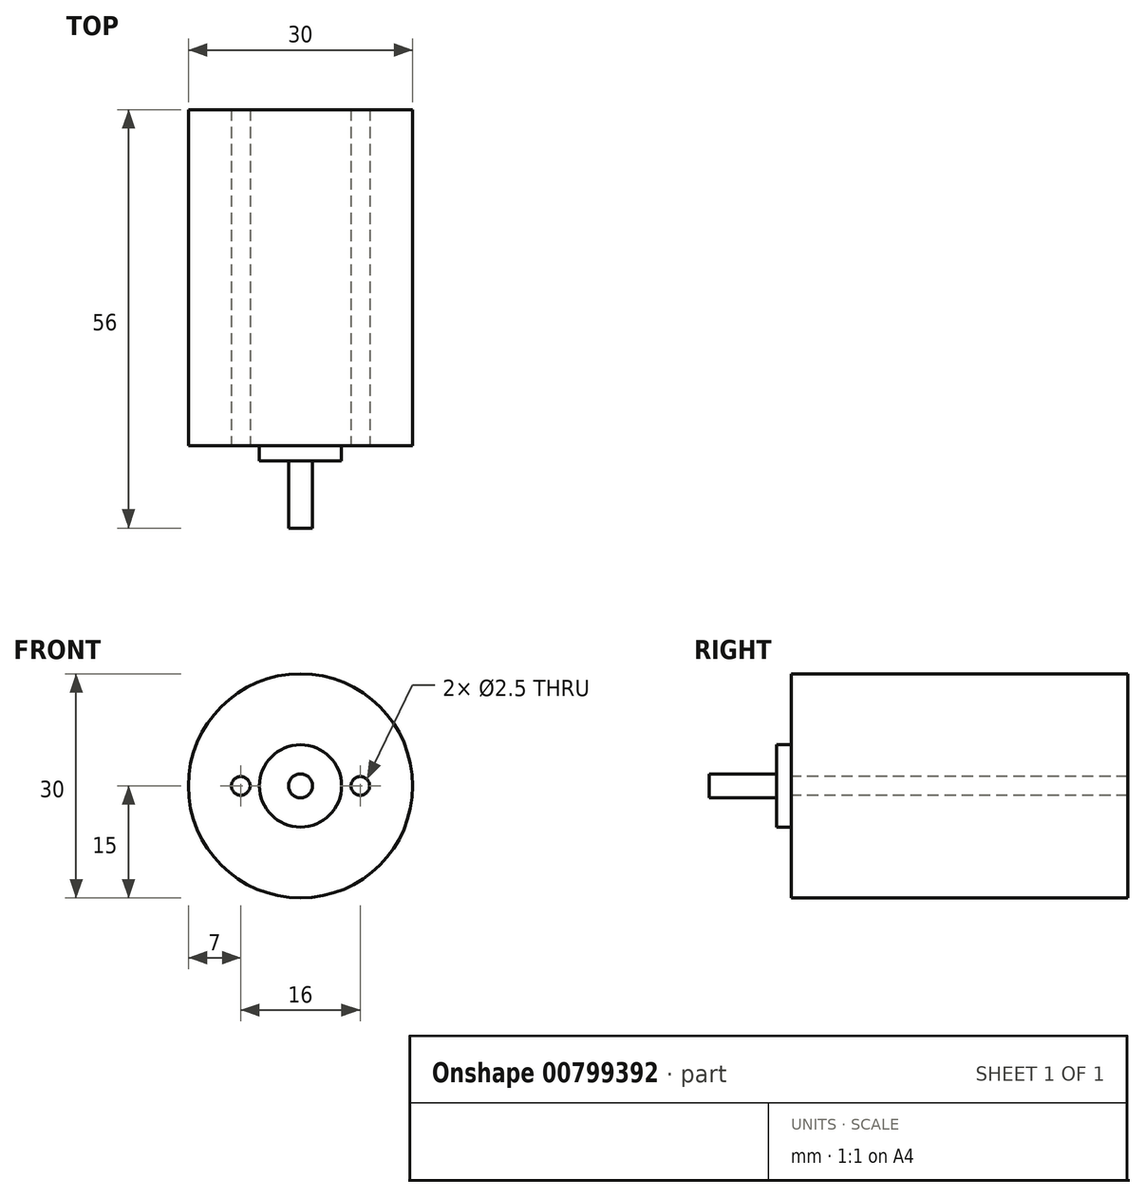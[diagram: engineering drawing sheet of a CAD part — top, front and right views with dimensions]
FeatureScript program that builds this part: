
annotation { "Feature Type Name" : "Feature", "Feature Type Description" : "" }
export const myFeature = defineFeature(function(context is Context, id is Id, definition is map)
    precondition{}
    {
        {
            var Q0;
            Q0=qCreatedBy(makeId("Front.planeOp"),FACE);
            var sketch = newSketch(context, id + "F0", { "sketchPlane" : qUnion([Q0])});
            skCircle(sketch, "E0", {"center": v(0, 0) * mm, "radius": 15 * mm});
            skCircle(sketch, "E1", {"center": v(0, 0) * mm, "radius": 5.5 * mm});
            skCircle(sketch, "E2", {"center": v(-8, 0) * mm, "radius": 1.25 * mm});
            skCircle(sketch, "E3.MirrorC", {"center": v(8, 0) * mm, "radius": 1.25 * mm});
            skSolve(sketch);
        }
        {
            var Q0;
            Q0=makeQuery(id+"F0.imprint","IMPRINT",FACE,{"disambiguationData":[TD([[makeQuery(id+"F0.imprint","IMPRINT",EDGE,{"derivedFrom":sQuery(id+"F0.wireOp",EDGE,"E0")}),1.0]])]});
            var Q1;
            Q1=makeQuery(id+"F0.imprint","IMPRINT",FACE,{"disambiguationData":[TD([[makeQuery(id+"F0.imprint","IMPRINT",EDGE,{"derivedFrom":sQuery(id+"F0.wireOp",EDGE,"E1")}),1.0]])]});
            extrude(context, id + "F1", {"entities" : qUnion([Q0, Q1]), "oppositeDirection" : true, "depth" : 45 * mm, "offsetDistance" : 25 * mm});
        }
        {
            var Q0;
            Q0=makeQuery(id+"F0.imprint","IMPRINT",FACE,{"disambiguationData":[TD([[makeQuery(id+"F0.imprint","IMPRINT",EDGE,{"derivedFrom":sQuery(id+"F0.wireOp",EDGE,"E1")}),1.0]])]});
            extrude(context, id + "F2", {"entities" : qUnion([Q0]), "operationType" : NewBodyOperationType.ADD, "depth" : 2 * mm, "offsetDistance" : 25 * mm});
        }
        {
            var Q0;
            Q0=makeQuery(id+"F2.opExtrude","CAP_FACE",FACE,{"disambiguationData":[OSD([sQuery(id+"F0.wireOp",EDGE,"E1")])],"isStart":false});
            var sketch = newSketch(context, id + "F3", { "sketchPlane" : qUnion([Q0])});
            skCircle(sketch, "E4", {"center": v(0, 0) * mm, "radius": 1.6 * mm});
            skSolve(sketch);
        }
        {
            var Q0;
            Q0=makeQuery(id+"F3.imprint","IMPRINT",FACE,{"disambiguationData":[TD([[makeQuery(id+"F3.imprint","IMPRINT",EDGE,{"derivedFrom":sQuery(id+"F3.wireOp",EDGE,"E4")}),1.0]])]});
            extrude(context, id + "F4", {"entities" : qUnion([Q0]), "operationType" : NewBodyOperationType.ADD, "depth" : 9 * mm, "offsetDistance" : 25 * mm});
        }
    });
